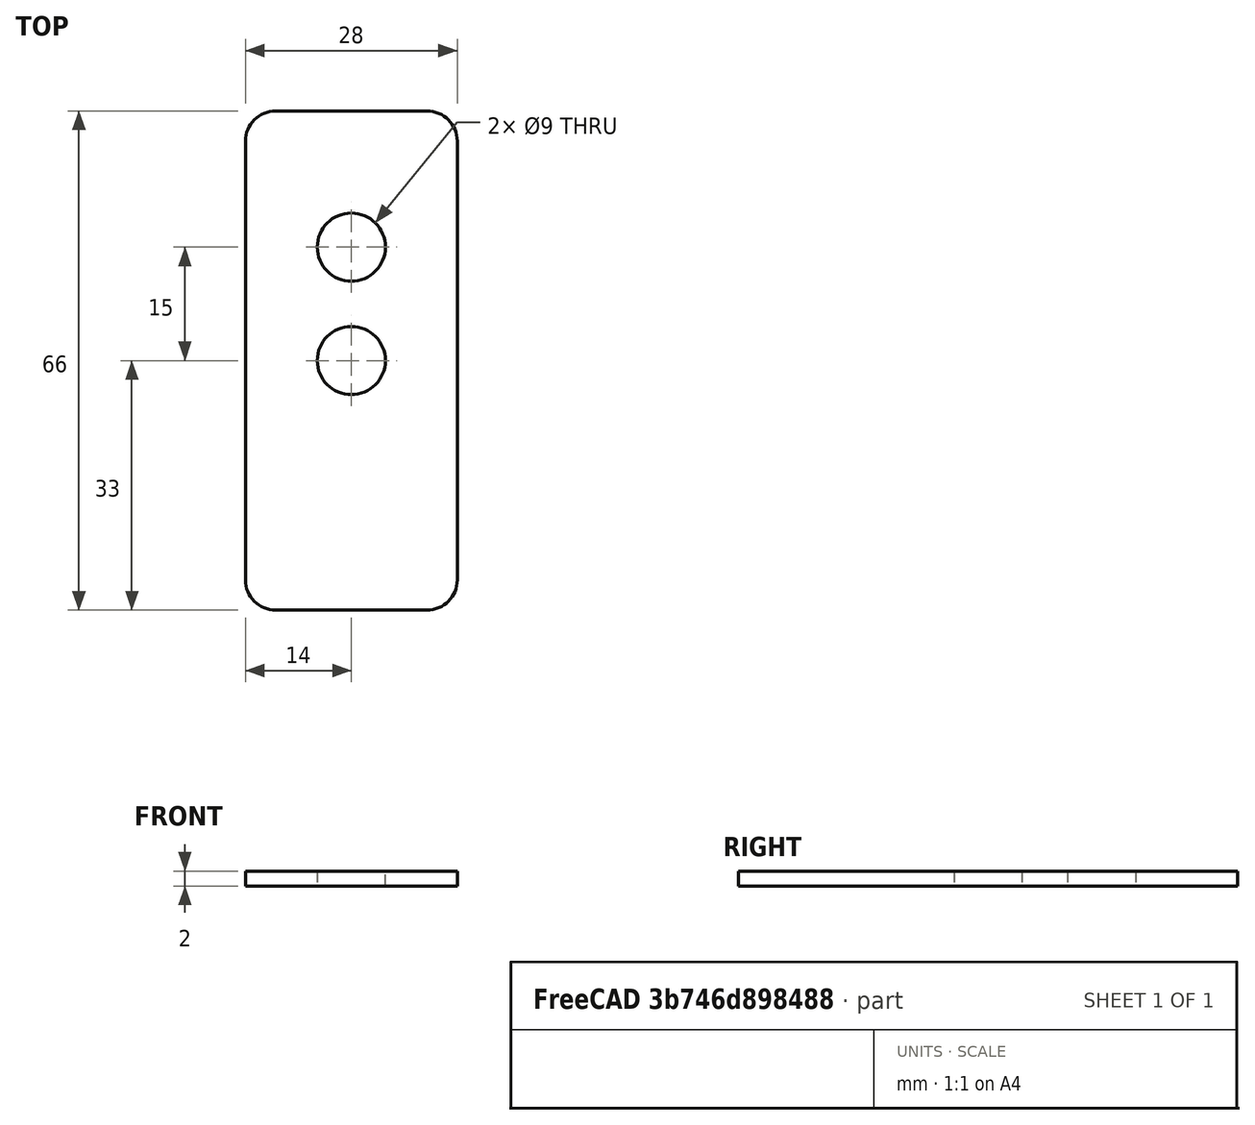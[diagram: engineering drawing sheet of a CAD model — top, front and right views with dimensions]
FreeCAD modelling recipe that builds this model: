
FCSTD DOCUMENT  (FreeCAD 0.21R33694 (Git))
Label: GabaritoCorteBorracha2
License: All rights reserved
LicenseURL: http://en.wikipedia.org/wiki/All_rights_reserved
objects: Sketcher::SketchObject×1, PartDesign::Pad×1, PartDesign::Body×1
note: 4 computed .brp shape members not serialized (recipe doc carries the construction recipe); baked Part::Feature solids carry a one-line shape summary decoded from their .brp

FEATURE [Sketcher::SketchObject] Sketch
  FullyConstrained = true
  MapMode = 5
  Support = -> [XY_Plane]
  sketch-geometry (10):
    g0: LineSegment StartX=-10 StartY=33 StartZ=0 EndX=10 EndY=33 EndZ=0
    g1: LineSegment StartX=14 StartY=29 StartZ=0 EndX=14 EndY=-29 EndZ=0
    g2: LineSegment StartX=10 StartY=-33 StartZ=0 EndX=-10 EndY=-33 EndZ=0
    g3: LineSegment StartX=-14 StartY=-29 StartZ=0 EndX=-14 EndY=29 EndZ=0
    g4: ArcOfCircle CenterX=-10 CenterY=29 CenterZ=0 NormalX=0 NormalY=0 NormalZ=1 AngleXU=0 Radius=4 StartAngle=1.5708 EndAngle=3.14159
    g5: ArcOfCircle CenterX=10 CenterY=29 CenterZ=0 NormalX=0 NormalY=0 NormalZ=1 AngleXU=0 Radius=4 StartAngle=-6.076e-12 EndAngle=1.5708
    g6: ArcOfCircle CenterX=10 CenterY=-29 CenterZ=0 NormalX=0 NormalY=0 NormalZ=1 AngleXU=0 Radius=4 StartAngle=4.71239 EndAngle=6.28319
    g7: ArcOfCircle CenterX=-10 CenterY=-29 CenterZ=0 NormalX=0 NormalY=0 NormalZ=1 AngleXU=0 Radius=4 StartAngle=3.14159 EndAngle=4.71239
    g8: Circle CenterX=0 CenterY=0 CenterZ=0 NormalX=0 NormalY=0 NormalZ=1 AngleXU=0 Radius=4.5
    g9: Circle CenterX=0 CenterY=15 CenterZ=0 NormalX=0 NormalY=0 NormalZ=1 AngleXU=0 Radius=4.5
  constraints (24):
    c: Horizontal(g2)
    c: Vertical(g3)
    c: Tangent(g0,g4) = 1.5708
    c: Tangent(g3,g4) = 1.5708
    c: Tangent(g0,g5) = 1.5708
    c: Tangent(g1,g5) = 1.5708
    c: Tangent(g1,g6) = 1.5708
    c: Tangent(g2,g6) = 1.5708
    c: Tangent(g2,g7) = 1.5708
    c: Tangent(g3,g7) = 1.5708
    c: Equal(g4,g5)
    c: Equal(g4,g6)
    c: Diameter(g4) = 8
    c: Horizontal(g0)
    c: Symmetric(g7,g6,g-2)
    c: DistanceY(g2,g0) = 66
    c: DistanceX(g3,g1) = 28
    c: Coincident(g8,g-1)
    c: Diameter(g8) = 9
    c: PointOnObject(g9,g-2)
    c: DistanceY(g8,g9) = 15
    c: Vertical(g1)
    c: Equal(g8,g9)
    c: DistanceY(g8,g0) = 33
FEATURE [PartDesign::Pad] Pad
  Direction = (0,0,1)
  Length = 2
  Length2 = 10
  Profile = -> Sketch
  ReferenceAxis = -> Sketch [N_Axis]
  Type = 0
FEATURE [PartDesign::Body] Body
  Group = -> [Sketch,Pad]
  Origin = -> Origin
  Tip = -> Pad
